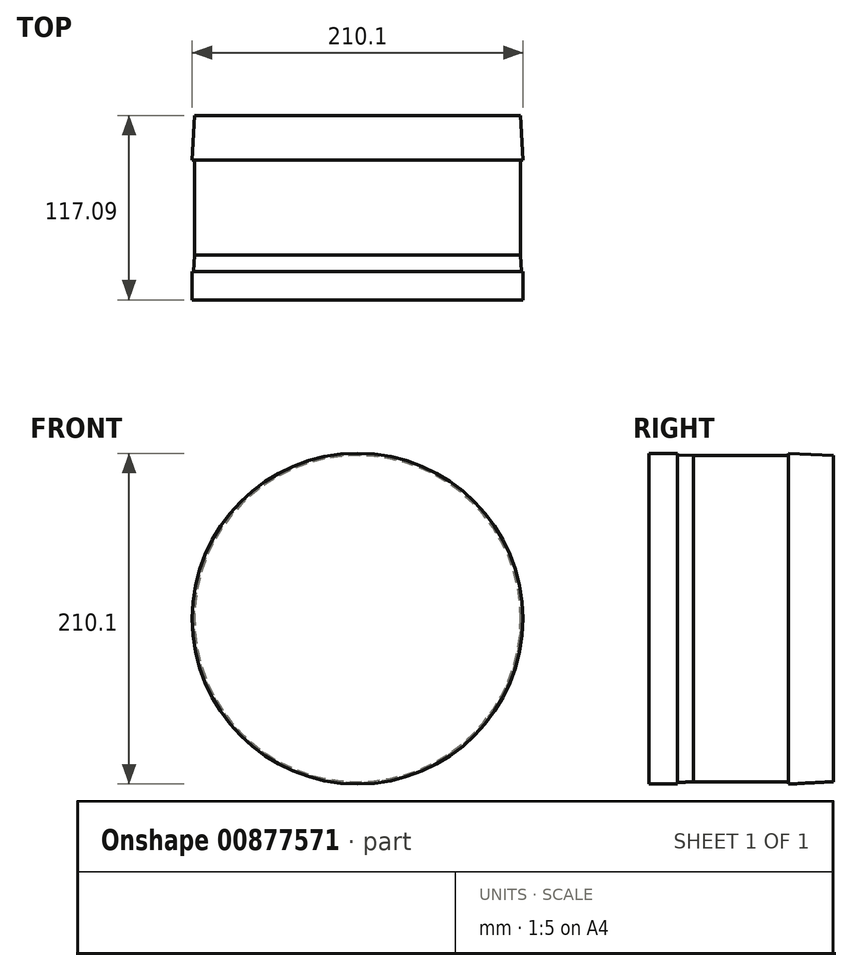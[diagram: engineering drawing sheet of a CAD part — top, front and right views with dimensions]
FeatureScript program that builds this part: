
annotation { "Feature Type Name" : "Feature", "Feature Type Description" : "" }
export const myFeature = defineFeature(function(context is Context, id is Id, definition is map)
    precondition{}
    {
        {
            var Q0;
            Q0=qCreatedBy(makeId("Front.planeOp"),FACE);
            var sketch = newSketch(context, id + "F0", { "sketchPlane" : qUnion([Q0])});
            skCircle(sketch, "E0", {"center": v(0, 0) * mm, "radius": 103.56 * mm});
            skSolve(sketch);
        }
        {
            var Q0;
            Q0=makeQuery(id+"F0.imprint","IMPRINT",FACE,{"disambiguationData":[TD([[makeQuery(id+"F0.imprint","IMPRINT",EDGE,{"derivedFrom":sQuery(id+"F0.wireOp",EDGE,"E0")}),1.0]])]});
            extrude(context, id + "F1", {"entities" : qUnion([Q0]), "depth" : 88.65 * mm, "offsetDistance" : 25.4 * mm});
        }
        {
            var Q0;
            Q0=qNothing();
            var sketch = newSketch(context, id + "F2", { "sketchPlane" : qUnion([Q0])});
            skSolve(sketch);
        }
        {
            var Q0;
            Q0 = qSketchRegion(id + "F2", true);
            var Q1;
            Q1=makeQuery(id+"F1.opExtrude","CAP_FACE",FACE,{"disambiguationData":[OSD([sQuery(id+"F0.wireOp",EDGE,"E0")])],"isStart":false});
            var Q2;
            Q2=makeQuery(id+"F1.opExtrude","CAP_FACE",FACE,{"disambiguationData":[OSD([sQuery(id+"F0.wireOp",EDGE,"E0")])],"isStart":true});
            extrude(context, id + "F3", {"entities" : qUnion([Q0, Q1, Q2]), "operationType" : NewBodyOperationType.ADD, "depth" : 28.45 * mm, "offsetDistance" : 25.4 * mm, "hasDraft" : true, "draftAngle" : 3 * degree});
        }
        {
            var Q0;
            {var subQ0=sQuery(id+"F0.wireOp",EDGE,"E0");Q0=makeQuery(id+"F3.opExtrude","CAP_FACE",FACE,{"disambiguationData":[OSD([subQ0]),TDD([makeQuery(id+"F1.opExtrude","CAP_FACE",FACE,{"disambiguationData":[OSD([subQ0])],"isStart":false})])],"isStart":false});}
            extrude(context, id + "F4", {"entities" : qUnion([Q0]), "operationType" : NewBodyOperationType.ADD, "oppositeDirection" : true, "depth" : 18.03 * mm, "offsetDistance" : 25.4 * mm});
        }
    });
